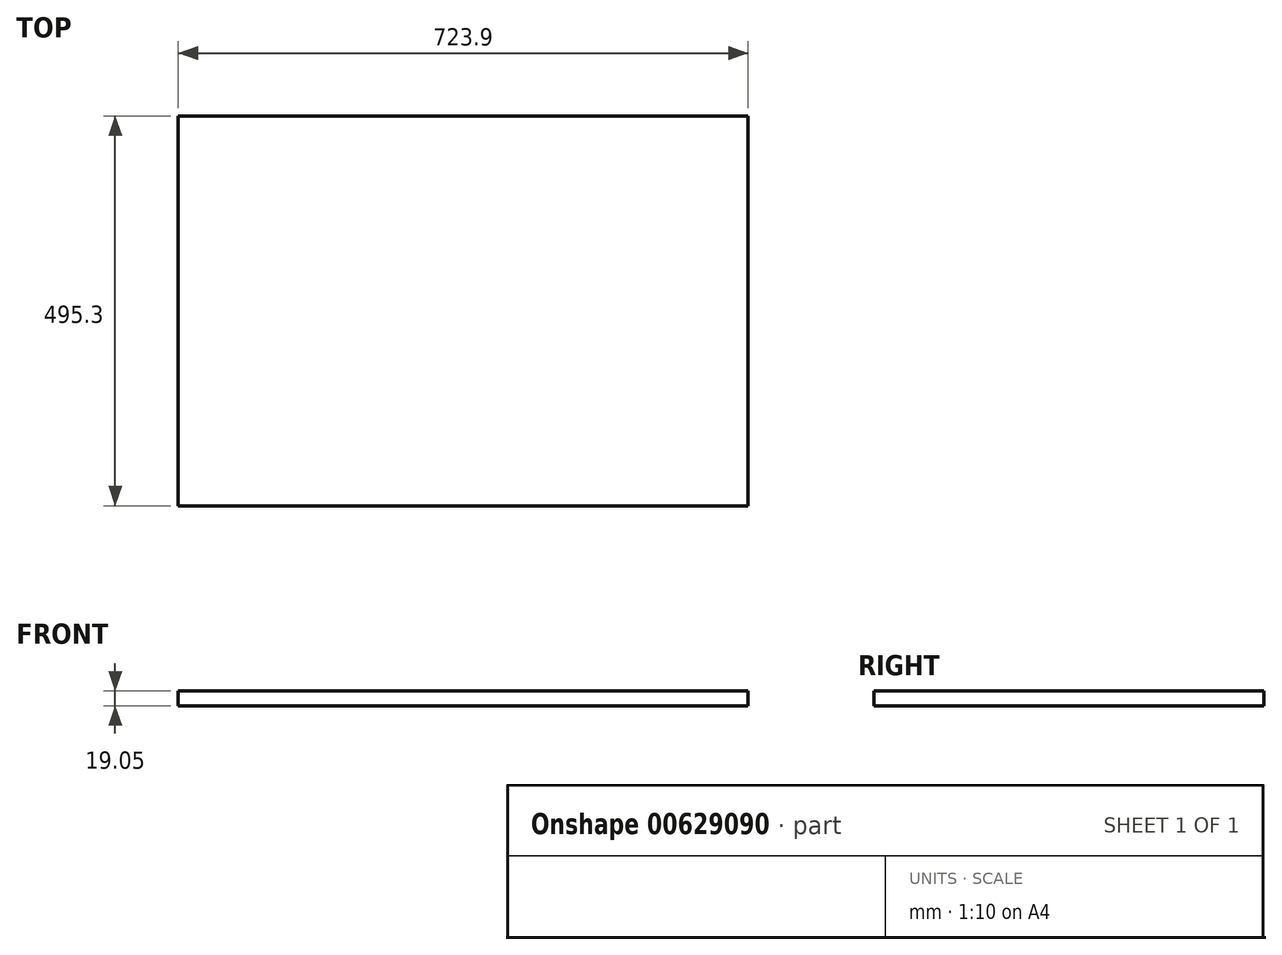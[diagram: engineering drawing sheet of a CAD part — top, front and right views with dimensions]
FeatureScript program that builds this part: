
annotation { "Feature Type Name" : "Feature", "Feature Type Description" : "" }
export const myFeature = defineFeature(function(context is Context, id is Id, definition is map)
    precondition{}
    {
        {
            var Q0;
            Q0=qCreatedBy(makeId("Top.planeOp"),FACE);
            var sketch = newSketch(context, id + "F0", { "sketchPlane" : qUnion([Q0])});
            skLineSegment(sketch, "E0.bottom", {"start": v(361.95, 247.65) * mm, "end": v(-361.95, 247.65) * mm});
            skLineSegment(sketch, "E0.top", {"start": v(361.95, -247.65) * mm, "end": v(-361.95, -247.65) * mm});
            skLineSegment(sketch, "E0.left", {"start": v(361.95, 247.65) * mm, "end": v(361.95, -247.65) * mm});
            skLineSegment(sketch, "E0.right", {"start": v(-361.95, 247.65) * mm, "end": v(-361.95, -247.65) * mm});
            skPoint(sketch, "E0.middle", {"position": v(0, 0) * mm});
            skSolve(sketch);
        }
        {
            var Q0;
            Q0=makeQuery(id+"F0.imprint","IMPRINT",FACE,{"disambiguationData":[TD([[makeQuery(id+"F0.imprint","IMPRINT",EDGE,{"derivedFrom":sQuery(id+"F0.wireOp",EDGE,"E0.bottom")}),1.0]])]});
            extrude(context, id + "F1", {"entities" : qUnion([Q0]), "depth" : 19.05 * mm, "offsetDistance" : 25.4 * mm});
        }
    });
